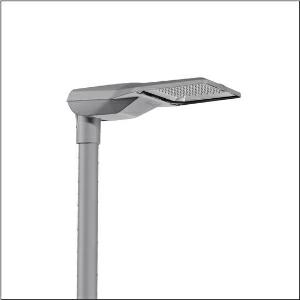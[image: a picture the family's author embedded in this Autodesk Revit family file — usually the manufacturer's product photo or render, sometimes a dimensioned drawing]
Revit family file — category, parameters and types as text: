
# Revit family: streetlight_sl_21_midi___st0_5a_5xe7b43a08nb_8726
name_source: partatom
category: Lighting Fixtures
units: mm (PartAtom-declared; Revit-internal decimal feet)

## family parameters
Cut with Voids When Loaded = No
Host = Face
Light Source = No
Part Type = Normal
Room Calculation Point = No
Round Connector Dimension = Use Diameter
Shared = No

## types (1)
- --- (1 x LED, 23710 lm, 151.2 W, 4000K)
    Apparent Load = 151 VA
    CIE Flux Codes = 43 76 97 100 100
    Color Rendering = 70
    Color Temperature = 4000K
    Default Elevation = 1800 mm
    Description = Streetlight SL 21 midi, mast luminaire, primary light control with lens, of PMMA, primary optical cover: cover, of toughened safety glass, transparent, light distribution: ST0.5a, light emission: direct distribution, primary light characteristic: asymmetric, installation type: post-top, side-entry, LED, 3G 1.5mm², High Power LED, rated luminous flux: 23.710lm, luminous efficacy: 157lm/W, light colour: 740, colour temperature: 4000K, control: overheat protection, constant luminous flux control, time-dependent luminous flux control, flexible luminous flux parameterisation, mains connection: 220..240V, AC, 50/60Hz, connection cable pre-assembled, cable length: 12,5m, wiring characteristics: H07RN-F, start of lifetime: 151W, end of service life: 157W, reduction: 71W, luminaire housing, of diecast aluminium, powder-coated, Siteco® metallic grey (DB 702S), corrosivity category C5 mid according to DIN EN ISO 12944, please order mast flange separately, inclination adjustable: 0°, 5°, 10°, 15°, sealing non-destructively replaceable, multi-level sealing system, length: 644mm, width: 335mm, height: 110mm, mast flange for spigot size: 42mm (side-entry): 5XC10008XM4, 60/48mm (side-entry/post-top): 5XC10108XM2, 76/60mm (side-entry/post-top): 5XC10108XM1, protection rating (complete): IP66, insulation class (complete): insulation class II (safety insulation), certification: CE, ENEC, ENEC+, VDE, impact resistance: IK09, permissible operating ambient temperature for outdoor applications: -40..+50°C, standard-compliant lighting for roads and squares, packaging unit: 1 piece

Light Distribution: ST0.5a
    Height = 111 mm
    Lamp = 1 x LED
    Lamp Light Flux = 23710 lm
    Lamp Power = 151.2 W
    Lamp count = 1
    Length = 644 mm
    Luminous efficacy = 157 lm/W
    Manufacturer = Siteco
    ModVariant = No
    Model = 5XE7B43A08NB
    Number of Poles = 1
    OnlyDefault = Yes
    Power Factor = 1
    Product Name = Streetlight SL 21 midi | ST0.5a
    Product group = mast luminaire | pylon top
    ProductGroupID = 6100
    Protection Class = Protection class II
    Protection Degree = IP 66
    RLX_Detail_Level = 1
    RLX_Emergency_Light_Flux = 0 lm
    RLX_Emergency_Type = 0
    RLX_Emergency_Type_DB = No
    RlxData = <blob elided: 101389 chars, md5=ebd8a298>
    Socket = socket
    Standby Power = 0 W
    System Light Flux = 23710 lm
    System Power = 151 W
    Type Comments = factory setting: luminous flux: 100 % | Output Level: 100 % | 802 mA
    Type Image = l_1004298.jpg
    URL = http://relux.com
    VarID = @adj_122013
    Voltage = 0 V
    Weight = 0.00 kg
    Width = 336 mm

## geometry (parser evidence)
native form markers: Blend x4, Sweep x10
no freeform markers — native parametric forms only
